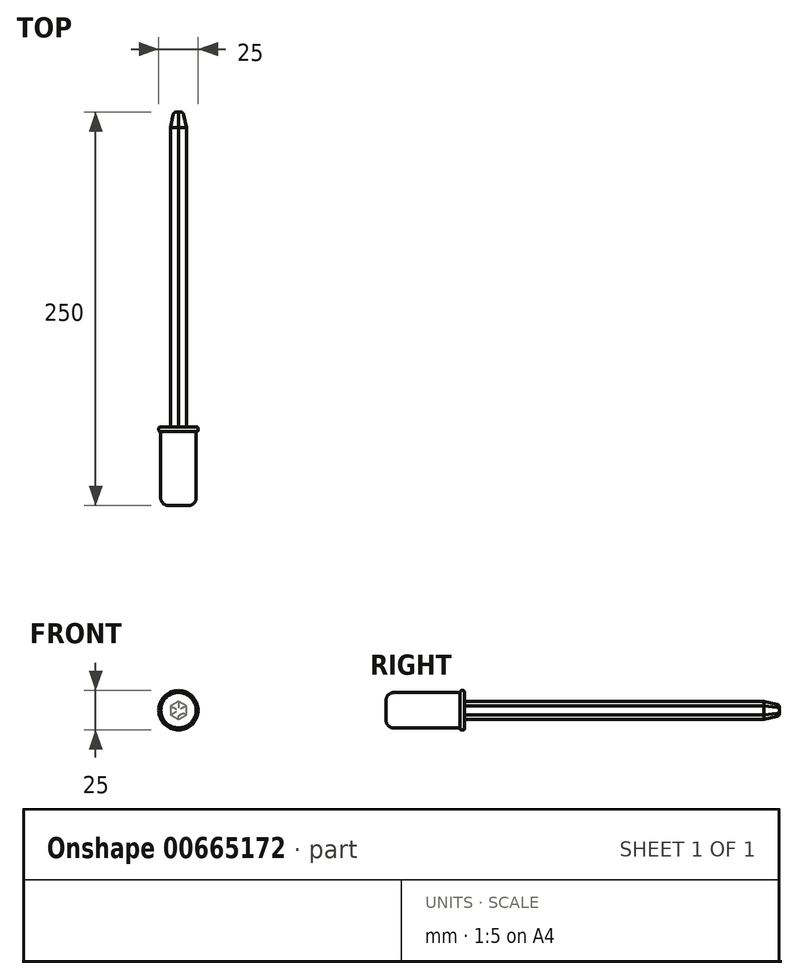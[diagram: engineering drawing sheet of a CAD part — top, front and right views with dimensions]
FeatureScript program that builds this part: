
annotation { "Feature Type Name" : "Feature", "Feature Type Description" : "" }
export const myFeature = defineFeature(function(context is Context, id is Id, definition is map)
    precondition{}
    {
        {
            var Q0;
            Q0=qCreatedBy(makeId("Front.planeOp"),FACE);
            var sketch = newSketch(context, id + "F0", { "sketchPlane" : qUnion([Q0])});
            skCircle(sketch, "E0", {"center": v(0, 0) * mm, "radius": 5 * mm});
            skLineSegment(sketch, "E1.0", {"start": v(5, 2.89) * mm, "end": v(5, -2.89) * mm});
            skLineSegment(sketch, "E1.1", {"start": v(5, -2.89) * mm, "end": v(0, -5.77) * mm});
            skLineSegment(sketch, "E1.2", {"start": v(0, -5.77) * mm, "end": v(-5, -2.89) * mm});
            skLineSegment(sketch, "E1.3", {"start": v(-5, -2.89) * mm, "end": v(-5, 2.89) * mm});
            skLineSegment(sketch, "E1.4", {"start": v(-5, 2.89) * mm, "end": v(0, 5.77) * mm});
            skLineSegment(sketch, "E1.5", {"start": v(0, 5.77) * mm, "end": v(5, 2.89) * mm});
            skPoint(sketch, "E1.0.midPoint", {"position": v(5, 0) * mm});
            skSolve(sketch);
        }
        {
            var Q0;
            Q0 = qSketchRegion(id + "F0", true);
            extrude(context, id + "F1", {"entities" : qUnion([Q0]), "depth" : 200 * mm, "offsetDistance" : 25 * mm});
        }
        {
            var Q0;
            Q0=makeQuery(id+"F1.opExtrude","CAP_FACE",FACE,{"disambiguationData":[OSD([sQuery(id+"F0.wireOp",EDGE,"E1.0"),sQuery(id+"F0.wireOp",EDGE,"E1.1"),sQuery(id+"F0.wireOp",EDGE,"E1.2"),sQuery(id+"F0.wireOp",EDGE,"E1.3"),sQuery(id+"F0.wireOp",EDGE,"E1.4"),sQuery(id+"F0.wireOp",EDGE,"E1.5")])],"isStart":false});
            var sketch = newSketch(context, id + "F2", { "sketchPlane" : qUnion([Q0])});
            skCircle(sketch, "E2", {"center": v(0, 0) * mm, "radius": 11.25 * mm});
            skSolve(sketch);
        }
        {
            var Q0;
            Q0 = qSketchRegion(id + "F2", true);
            extrude(context, id + "F3", {"entities" : qUnion([Q0]), "operationType" : NewBodyOperationType.ADD, "depth" : 50 * mm, "offsetDistance" : 25 * mm});
        }
        {
            var Q0;
            Q0=makeQuery(id+"F3.opExtrude","CAP_FACE",FACE,{"disambiguationData":[OSD([sQuery(id+"F2.wireOp",EDGE,"E2")])],"isStart":true});
            var sketch = newSketch(context, id + "F4", { "sketchPlane" : qUnion([Q0])});
            skCircle(sketch, "E3", {"center": v(0, 0) * mm, "radius": 12.5 * mm});
            skSolve(sketch);
        }
        {
            var Q0;
            Q0 = qSketchRegion(id + "F4", true);
            extrude(context, id + "F5", {"entities" : qUnion([Q0]), "operationType" : NewBodyOperationType.ADD, "oppositeDirection" : true, "depth" : 3 * mm, "offsetDistance" : 25 * mm});
        }
        {
            var Q0;
            Q0=makeQuery(id+"F5.opExtrude","CAP_EDGE",EDGE,{"disambiguationData":[OSD([sQuery(id+"F4.wireOp",EDGE,"E3")])],"isStart":false});
            var Q1;
            Q1=makeQuery(id+"F5.opExtrude","CAP_EDGE",EDGE,{"disambiguationData":[OSD([sQuery(id+"F4.wireOp",EDGE,"E3")])],"isStart":true});
            fillet(context, id + "F6", {"entities" : qUnion([Q0, Q1]), "radius" : 1 * mm, "tangentPropagation" : true, "allowEdgeOverflow" : false});
        }
        {
            var Q0;
            Q0=makeQuery(id+"F3.opExtrude","CAP_EDGE",EDGE,{"disambiguationData":[OSD([sQuery(id+"F2.wireOp",EDGE,"E2")])],"isStart":false});
            fillet(context, id + "F7", {"entities" : qUnion([Q0]), "radius" : 5 * mm, "tangentPropagation" : true, "allowEdgeOverflow" : false});
        }
        {
            var Q0;
            Q0=makeQuery(id+"F1.opExtrude","CAP_FACE",FACE,{"disambiguationData":[OSD([sQuery(id+"F0.wireOp",EDGE,"E1.0"),sQuery(id+"F0.wireOp",EDGE,"E1.1"),sQuery(id+"F0.wireOp",EDGE,"E1.2"),sQuery(id+"F0.wireOp",EDGE,"E1.3"),sQuery(id+"F0.wireOp",EDGE,"E1.4"),sQuery(id+"F0.wireOp",EDGE,"E1.5")])],"isStart":true});
            chamfer(context, id + "F8", {"entities" : qUnion([Q0]), "chamferType" : ChamferType.TWO_OFFSETS, "width1" : 2 * mm, "oppositeDirection" : false, "width2" : 10 * mm, "tangentPropagation" : true});
        }
        {
            var Q0;
            {var subQ0=sQuery(id+"F0.wireOp",EDGE,"E1.0");Q0=makeQuery(id+"F8.opChamfer","BLEND_EDGE",EDGE,{"blendedFrom":[makeQuery(id+"F1.opExtrude","CAP_EDGE",EDGE,{"disambiguationData":[OSD([subQ0])],"isStart":true}),makeQuery(id+"F1.opExtrude","CAP_FACE",FACE,{"disambiguationData":[OSD([subQ0,sQuery(id+"F0.wireOp",EDGE,"E1.1"),sQuery(id+"F0.wireOp",EDGE,"E1.2"),sQuery(id+"F0.wireOp",EDGE,"E1.3"),sQuery(id+"F0.wireOp",EDGE,"E1.4"),sQuery(id+"F0.wireOp",EDGE,"E1.5")])],"isStart":true})],"blendedInto":[makeQuery(id+"F1.opExtrude","CAP_FACE",FACE,{"disambiguationData":[OSD([subQ0,sQuery(id+"F0.wireOp",EDGE,"E1.1"),sQuery(id+"F0.wireOp",EDGE,"E1.2"),sQuery(id+"F0.wireOp",EDGE,"E1.3"),sQuery(id+"F0.wireOp",EDGE,"E1.4"),sQuery(id+"F0.wireOp",EDGE,"E1.5")])],"isStart":true})]});}
            var Q1;
            {var subQ0=sQuery(id+"F0.wireOp",EDGE,"E1.5");Q1=makeQuery(id+"F8.opChamfer","BLEND_EDGE",EDGE,{"blendedFrom":[makeQuery(id+"F1.opExtrude","CAP_EDGE",EDGE,{"disambiguationData":[OSD([subQ0])],"isStart":true}),makeQuery(id+"F1.opExtrude","CAP_FACE",FACE,{"disambiguationData":[OSD([sQuery(id+"F0.wireOp",EDGE,"E1.0"),sQuery(id+"F0.wireOp",EDGE,"E1.1"),sQuery(id+"F0.wireOp",EDGE,"E1.2"),sQuery(id+"F0.wireOp",EDGE,"E1.3"),sQuery(id+"F0.wireOp",EDGE,"E1.4"),subQ0])],"isStart":true})],"blendedInto":[makeQuery(id+"F1.opExtrude","CAP_FACE",FACE,{"disambiguationData":[OSD([sQuery(id+"F0.wireOp",EDGE,"E1.0"),sQuery(id+"F0.wireOp",EDGE,"E1.1"),sQuery(id+"F0.wireOp",EDGE,"E1.2"),sQuery(id+"F0.wireOp",EDGE,"E1.3"),sQuery(id+"F0.wireOp",EDGE,"E1.4"),subQ0])],"isStart":true})]});}
            var Q2;
            {var subQ0=sQuery(id+"F0.wireOp",EDGE,"E1.4");Q2=makeQuery(id+"F8.opChamfer","BLEND_EDGE",EDGE,{"blendedFrom":[makeQuery(id+"F1.opExtrude","CAP_EDGE",EDGE,{"disambiguationData":[OSD([subQ0])],"isStart":true}),makeQuery(id+"F1.opExtrude","CAP_FACE",FACE,{"disambiguationData":[OSD([sQuery(id+"F0.wireOp",EDGE,"E1.0"),sQuery(id+"F0.wireOp",EDGE,"E1.1"),sQuery(id+"F0.wireOp",EDGE,"E1.2"),sQuery(id+"F0.wireOp",EDGE,"E1.3"),subQ0,sQuery(id+"F0.wireOp",EDGE,"E1.5")])],"isStart":true})],"blendedInto":[makeQuery(id+"F1.opExtrude","CAP_FACE",FACE,{"disambiguationData":[OSD([sQuery(id+"F0.wireOp",EDGE,"E1.0"),sQuery(id+"F0.wireOp",EDGE,"E1.1"),sQuery(id+"F0.wireOp",EDGE,"E1.2"),sQuery(id+"F0.wireOp",EDGE,"E1.3"),subQ0,sQuery(id+"F0.wireOp",EDGE,"E1.5")])],"isStart":true})]});}
            var Q3;
            {var subQ0=sQuery(id+"F0.wireOp",EDGE,"E1.3");Q3=makeQuery(id+"F8.opChamfer","BLEND_EDGE",EDGE,{"blendedFrom":[makeQuery(id+"F1.opExtrude","CAP_EDGE",EDGE,{"disambiguationData":[OSD([subQ0])],"isStart":true}),makeQuery(id+"F1.opExtrude","CAP_FACE",FACE,{"disambiguationData":[OSD([sQuery(id+"F0.wireOp",EDGE,"E1.0"),sQuery(id+"F0.wireOp",EDGE,"E1.1"),sQuery(id+"F0.wireOp",EDGE,"E1.2"),subQ0,sQuery(id+"F0.wireOp",EDGE,"E1.4"),sQuery(id+"F0.wireOp",EDGE,"E1.5")])],"isStart":true})],"blendedInto":[makeQuery(id+"F1.opExtrude","CAP_FACE",FACE,{"disambiguationData":[OSD([sQuery(id+"F0.wireOp",EDGE,"E1.0"),sQuery(id+"F0.wireOp",EDGE,"E1.1"),sQuery(id+"F0.wireOp",EDGE,"E1.2"),subQ0,sQuery(id+"F0.wireOp",EDGE,"E1.4"),sQuery(id+"F0.wireOp",EDGE,"E1.5")])],"isStart":true})]});}
            var Q4;
            {var subQ0=sQuery(id+"F0.wireOp",EDGE,"E1.2");Q4=makeQuery(id+"F8.opChamfer","BLEND_EDGE",EDGE,{"blendedFrom":[makeQuery(id+"F1.opExtrude","CAP_EDGE",EDGE,{"disambiguationData":[OSD([subQ0])],"isStart":true}),makeQuery(id+"F1.opExtrude","CAP_FACE",FACE,{"disambiguationData":[OSD([sQuery(id+"F0.wireOp",EDGE,"E1.0"),sQuery(id+"F0.wireOp",EDGE,"E1.1"),subQ0,sQuery(id+"F0.wireOp",EDGE,"E1.3"),sQuery(id+"F0.wireOp",EDGE,"E1.4"),sQuery(id+"F0.wireOp",EDGE,"E1.5")])],"isStart":true})],"blendedInto":[makeQuery(id+"F1.opExtrude","CAP_FACE",FACE,{"disambiguationData":[OSD([sQuery(id+"F0.wireOp",EDGE,"E1.0"),sQuery(id+"F0.wireOp",EDGE,"E1.1"),subQ0,sQuery(id+"F0.wireOp",EDGE,"E1.3"),sQuery(id+"F0.wireOp",EDGE,"E1.4"),sQuery(id+"F0.wireOp",EDGE,"E1.5")])],"isStart":true})]});}
            fillet(context, id + "F9", {"entities" : qUnion([Q0, Q1, Q2, Q3, Q4]), "radius" : 2 * mm, "tangentPropagation" : true, "allowEdgeOverflow" : false});
        }
    });
